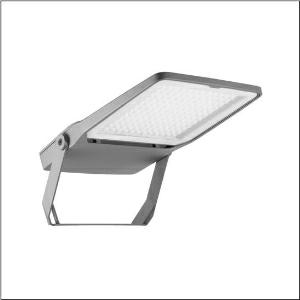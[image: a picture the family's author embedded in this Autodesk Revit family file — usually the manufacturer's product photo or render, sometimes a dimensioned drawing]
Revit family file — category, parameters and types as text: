
# Revit family: floodlight_fl_20_midi___pl43_5xa7682e3a1ac_f2b2
name_source: partatom
category: Lighting Fixtures
units: mm (PartAtom-declared; Revit-internal decimal feet)

## family parameters
Cut with Voids When Loaded = No
Host = Face
Light Source = No
Part Type = Normal
Room Calculation Point = No
Round Connector Dimension = Use Diameter
Shared = No

## types (1)
- --- (1 x LED 5000K / CRI = 70 (unbekannt), 28900 lm, 5000K)
    Apparent Load = 208 VA
    CIE Flux Codes = 32 74 99 100 100
    Color Rendering = 70
    Color Temperature = 5000K
    Default Elevation = 1800 mm
    Description = Floodlight FL 20 midi, floodlight, primary light control with lens, of plastic, primary optical cover: protective disc, of toughened safety glass, transparent, light distribution: PL43, light emission: direct distribution, primary light characteristic: asymmetric, installation type: surface-mounted, LED, High Power LED, rated luminous flux: 28.900lm, luminous efficacy: 139lm/W, light colour: 750, colour temperature: 5000K, control gear: ECG Plus, control: flexible luminous flux parameterisation, time-dependent luminous flux control, digital communication interface, power reduction, overheat protection, electronic power reduction, with terminal, 5-pole, max. 2.5mm², mains connection: 220..240V, AC, 50/60Hz, rated input power: 208W, LED unit, of diecast aluminium, powder-coated, Siteco® metallic grey (DB 702S), corrosivity category C5 mid according to DIN EN ISO 12944, incl. 1x M20 cable gland for cable Ø 6.5..12mm, length: 654mm, width: 450mm, height: 76mm, housing frame, of diecast aluminium, powder-coated, Siteco® metallic grey (DB 702S), mounting bracket, of steel, powder-coated, Siteco® metallic grey (DB 702S), DALI, protection rating (complete): IP66, insulation class (complete): insulation class II (safety insulation), certification: CE, ENEC, VDE, protection symbol: D, permissible operating ambient temperature: -40..+40°C, permissible operating ambient temperature for outdoor applications: -40..+50°C, standard: DIN EN 12944, packaging unit: 1 piece

Light Distribution: PL43
    Height = 76 mm
    Lamp = 1 x LED 5000K / CRI >= 70 (unbekannt)
    Lamp Light Flux = 28900 lm
    Lamp count = 1
    Length = 672 mm
    Luminous efficacy = 139 lm/W
    Manufacturer = Siteco
    ModVariant = No
    Model = 5XA7682E3A1AC
    Mounting Place = Wall
    Mounting Type = Surface mounted
    Number of Poles = 1
    OnlyDefault = Yes
    Power Factor = 1
    Product Name = Floodlight FL 20 midi | PL43
    Product group = floodlight | wall mounted
    ProductGroupID = 2001
    Protection Class = Protection class II
    Protection Degree = IP 66
    RLX_Detail_Level = 1
    RLX_Emergency_Light_Flux = 0 lm
    RLX_Emergency_Type = 0
    RLX_Emergency_Type_DB = No
    RlxData = <blob elided: 97733 chars, md5=089b071a>
    Socket = socket
    Standby Power = 0 W
    System Light Flux = 28900 lm
    System Power = 208 W
    Type Comments = factory setting: luminous flux: 100 % | dim-lin: 254 | 484 mA
    Type Image = l_1005943.jpg
    URL = http://relux.com
    VarID = @adj_148221
    Voltage = 0 V
    Weight = 0.00 kg
    Width = 450 mm

## geometry (parser evidence)
native form markers: Blend x4, Sweep x10
no freeform markers — native parametric forms only
